FCSTD DOCUMENT  (FreeCAD 0.16R)
Label: CommCopy
License: All rights reserved
LicenseURL: http://en.wikipedia.org/wiki/All_rights_reserved
objects: Sketcher::SketchObject×1
note: 1 computed .brp shape members not serialized (recipe doc carries the construction recipe); baked Part::Feature solids carry a one-line shape summary decoded from their .brp

FEATURE [Sketcher::SketchObject] Sketch
  sketch-geometry (29):
    g0: Circle CenterX=-374.166 CenterY=256 CenterZ=0 NormalX=0 NormalY=0 NormalZ=1 Radius=256
    g1: Circle CenterX=479.211 CenterY=256 CenterZ=0 NormalX=0 NormalY=0 NormalZ=1 Radius=256
    g2: Circle CenterX=0 CenterY=231 CenterZ=0 NormalX=0 NormalY=0 NormalZ=1 Radius=18
    g3: Circle CenterX=306.823 CenterY=722.02 CenterZ=0 NormalX=0 NormalY=0 NormalZ=1 Radius=11.1
    g4: LineSegment StartX=479.211 StartY=256 StartZ=0 EndX=384.692 EndY=489.943 EndZ=0
    g5: LineSegment StartX=0 StartY=231 StartZ=0 EndX=-93.5589 EndY=537.018 EndZ=0
    g6: Circle [constr] CenterX=0 CenterY=231 CenterZ=0 NormalX=0 NormalY=0 NormalZ=1 Radius=115
    g7: LineSegment StartX=476.863 StartY=208.422 StartZ=0 EndX=241.097 EndY=791.963 EndZ=0
    g8: LineSegment [constr] StartX=479.211 StartY=256 StartZ=0 EndX=479.211 EndY=0 EndZ=0
    g9: LineSegment [constr] StartX=476.863 StartY=208.422 StartZ=0 EndX=564.128 EndY=-7.56571 EndZ=0
    g10: LineSegment [constr] StartX=318.061 StartY=694.204 StartZ=0 EndX=284.254 EndY=685.146 EndZ=0
    g11: Circle [constr] CenterX=284.254 CenterY=685.146 CenterZ=0 NormalX=0 NormalY=0 NormalZ=1 Radius=19
    g12: Circle [constr] CenterX=306.465 CenterY=630.172 CenterZ=0 NormalX=0 NormalY=0 NormalZ=1 Radius=8
    g13: Circle [constr] CenterX=327.443 CenterY=578.249 CenterZ=0 NormalX=0 NormalY=0 NormalZ=1 Radius=48
    g14: Circle [constr] CenterX=348.046 CenterY=527.254 CenterZ=0 NormalX=0 NormalY=0 NormalZ=1 Radius=7
    g15: Circle [constr] CenterX=405.923 CenterY=384.004 CenterZ=0 NormalX=0 NormalY=0 NormalZ=1 Radius=147.5
    g16: LineSegment [constr] StartX=-374.166 StartY=256 StartZ=0 EndX=479.211 EndY=256 EndZ=0
    g17: LineSegment StartX=-374.166 StartY=256 StartZ=0 EndX=-79.2892 EndY=490.343 EndZ=0
    g18: LineSegment StartX=-79.2892 StartY=490.343 StartZ=0 EndX=317.637 EndY=602.519 EndZ=0
    g19: LineSegment StartX=0 StartY=231 StartZ=0 EndX=337.844 EndY=552.505 EndZ=0
    g20: LineSegment [constr] StartX=479.211 StartY=0 StartZ=0 EndX=561.071 EndY=0 EndZ=0
    g21: LineSegment [constr] StartX=0 StartY=231 StartZ=0 EndX=306.823 EndY=722.02 EndZ=0
    g22: LineSegment [constr] StartX=-374.166 StartY=256 StartZ=0 EndX=0 EndY=231 EndZ=0
    g23: LineSegment [constr] StartX=306.823 StartY=722.02 StartZ=0 EndX=318.061 EndY=694.204 EndZ=0
    g24: Circle [constr] CenterX=297.42 CenterY=652.559 CenterZ=0 NormalX=0 NormalY=0 NormalZ=1 Radius=16.1456
    g25: LineSegment [constr] StartX=0 StartY=231 StartZ=0 EndX=345.424 EndY=533.745 EndZ=0
    g26: LineSegment [constr] StartX=345.424 StartY=533.745 StartZ=0 EndX=457.515 EndY=256.6 EndZ=0
    g27: LineSegment [constr] StartX=0 StartY=231 StartZ=0 EndX=457.515 EndY=256.6 EndZ=0
    g28: LineSegment StartX=347.33 StartY=534.563 StartZ=0 EndX=459.539 EndY=256 EndZ=0
  constraints (73):
    c: Radius(g0) = 256
    c: Equal(g0,g1)
    c: Radius(g2) = 18
    c: Tangent(g1,g-1)
    c: Tangent(g0,g-1)
    c: Radius(g3) = 11.1
    c: Distance(g2,g3) = 579
    c: Coincident(g4,g1)
    c: Angle(g4) = 1.95477
    c: Angle(g5) = 1.8675
    c: Coincident(g5,g2)
    c: Radius(g6) = 115
    c: Coincident(g6,g2)
    c: Distance(g2,g0) = 375
    c: Parallel(g7,g4)
    c: Distance(g7,g4) = 20
    c: Coincident(g8,g1)
    c: Vertical(g8)
    c: Coincident(g9,g7)
    c: Parallel(g9,g7)
    c: PointOnObject(g10,g7)
    c: Coincident(g11,g10)
    c: Radius(g12) = 8
    c: PointOnObject(g12,g7)
    c: PointOnObject(g13,g7)
    c: Tangent(g13,g12)
    c: Radius(g14) = 7
    c: PointOnObject(g14,g7)
    c: Tangent(g14,g13)
    c: PointOnObject(g1,g15)
    c: PointOnObject(g15,g7)
    c: Radius(g15) = 147.5
    c: Tangent(g14,g15)
    c: Coincident(g16,g0)
    c: Coincident(g16,g1)
    c: Coincident(g17,g0)
    c: PointOnObject(g17,g5)
    c: Coincident(g18,g17)
    c: PointOnObject(g18,g7)
    c: Coincident(g19,g2)
    c: PointOnObject(g19,g7)
    c: PointOnObject(g20,g8)
    c: PointOnObject(g20,g9)
    c: Horizontal(g20)
    c: Coincident(g8,g20)
    c: PointOnObject(g8,g-1)
    c: Distance(g5) = 320
    c: Distance(g2,g16) = 25
    c: Coincident(g21,g2)
    c: Angle(g21) = 1.01229
    c: Distance(g10) = 35
    c: Coincident(g22,g0)
    c: Coincident(g22,g2)
    c: PointOnObject(g2,g-2)
    c: Angle(g7,g10) = 1.44862
    c: Coincident(g23,g10)
    c: Coincident(g21,g23)
    c: Coincident(g3,g21)
    c: Distance(g23) = 30
    c: Parallel(g23,g7)
    c: Radius(g13) = 48
    c: Radius(g11) = 19
    c: PointOnObject(g24,g7)
    c: Tangent(g24,g12)
    c: Tangent(g24,g11)
    c: Coincident(g25,g2)
    c: PointOnObject(g25,g13)
    c: PointOnObject(g25,g7)
    c: Coincident(g27,g2)
    c: Coincident(g27,g26)
    c: Distance(g25) = 459.317
    c: PointOnObject(g28,g13)
    c: PointOnObject(g28,g16)
